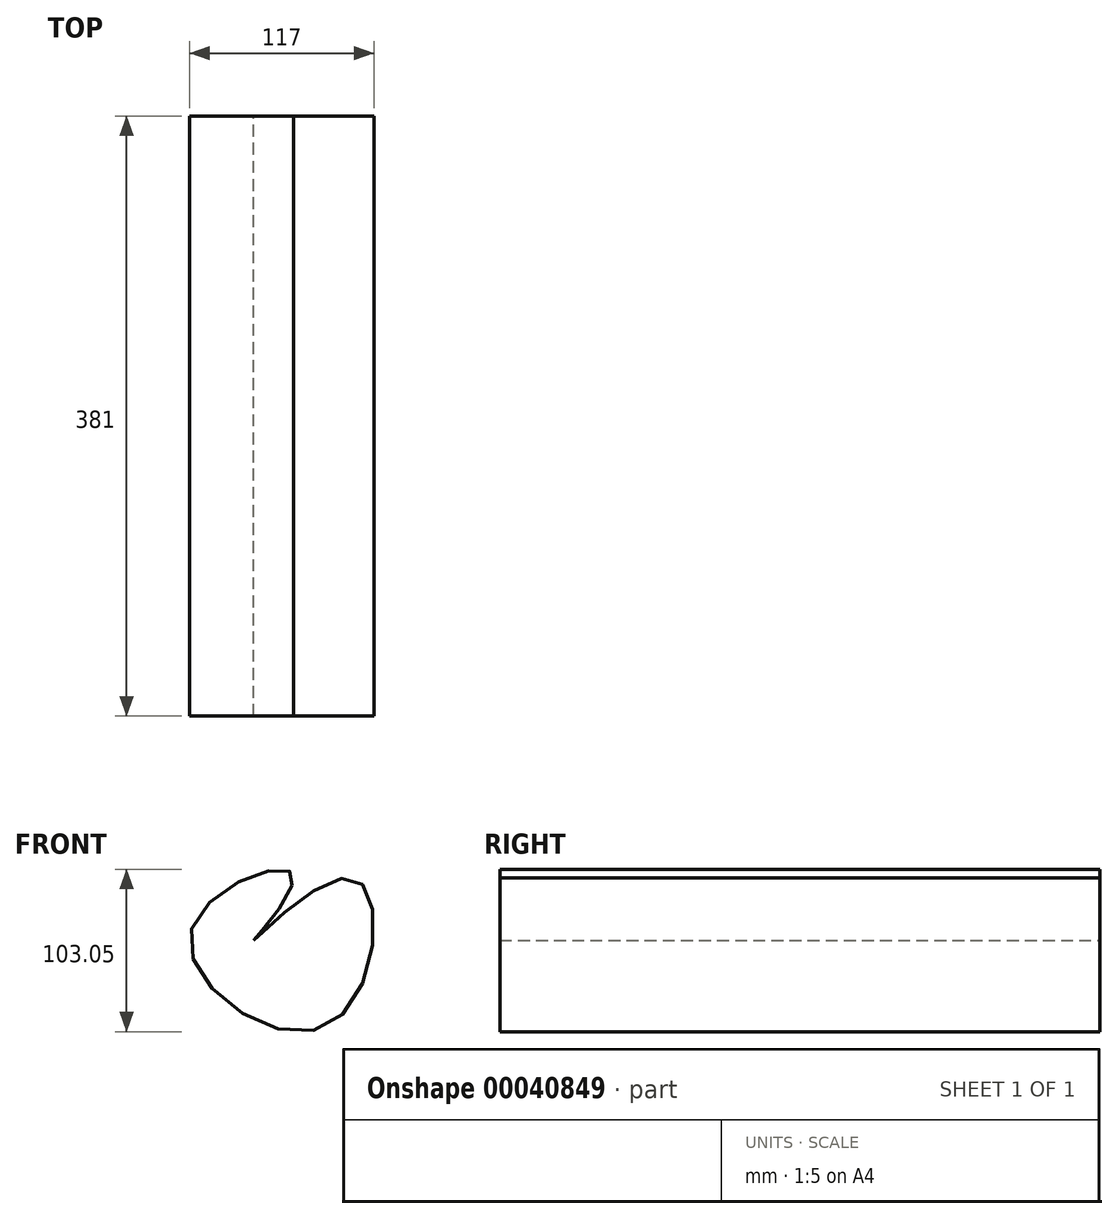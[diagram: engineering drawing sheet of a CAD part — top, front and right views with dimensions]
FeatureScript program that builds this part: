
annotation { "Feature Type Name" : "Feature", "Feature Type Description" : "" }
export const myFeature = defineFeature(function(context is Context, id is Id, definition is map)
    precondition{}
    {
        {
            var Q0;
            Q0=qCreatedBy(makeId("Front.planeOp"),FACE);
            var sketch = newSketch(context, id + "F0", { "sketchPlane" : qUnion([Q0])});
            skFitSpline(sketch, "E0", {"points": [v(0, 0) * mm, v(24.94, 41.62) * mm, v(-40.08, 5.46) * mm, v(47.08, -53.95) * mm, v(63.06, 39.37) * mm, v(0, 0) * mm]});
            skSolve(sketch);
        }
        {
            var Q0;
            Q0=makeQuery(id+"F0.imprint","IMPRINT",FACE,{"disambiguationData":[TD([[makeQuery(id+"F0.imprint","IMPRINT",EDGE,{"derivedFrom":sQuery(id+"F0.wireOp",EDGE,"E0")}),1.0]])]});
            extrude(context, id + "F1", {"entities" : qUnion([Q0]), "depth" : 381 * mm});
        }
    });
